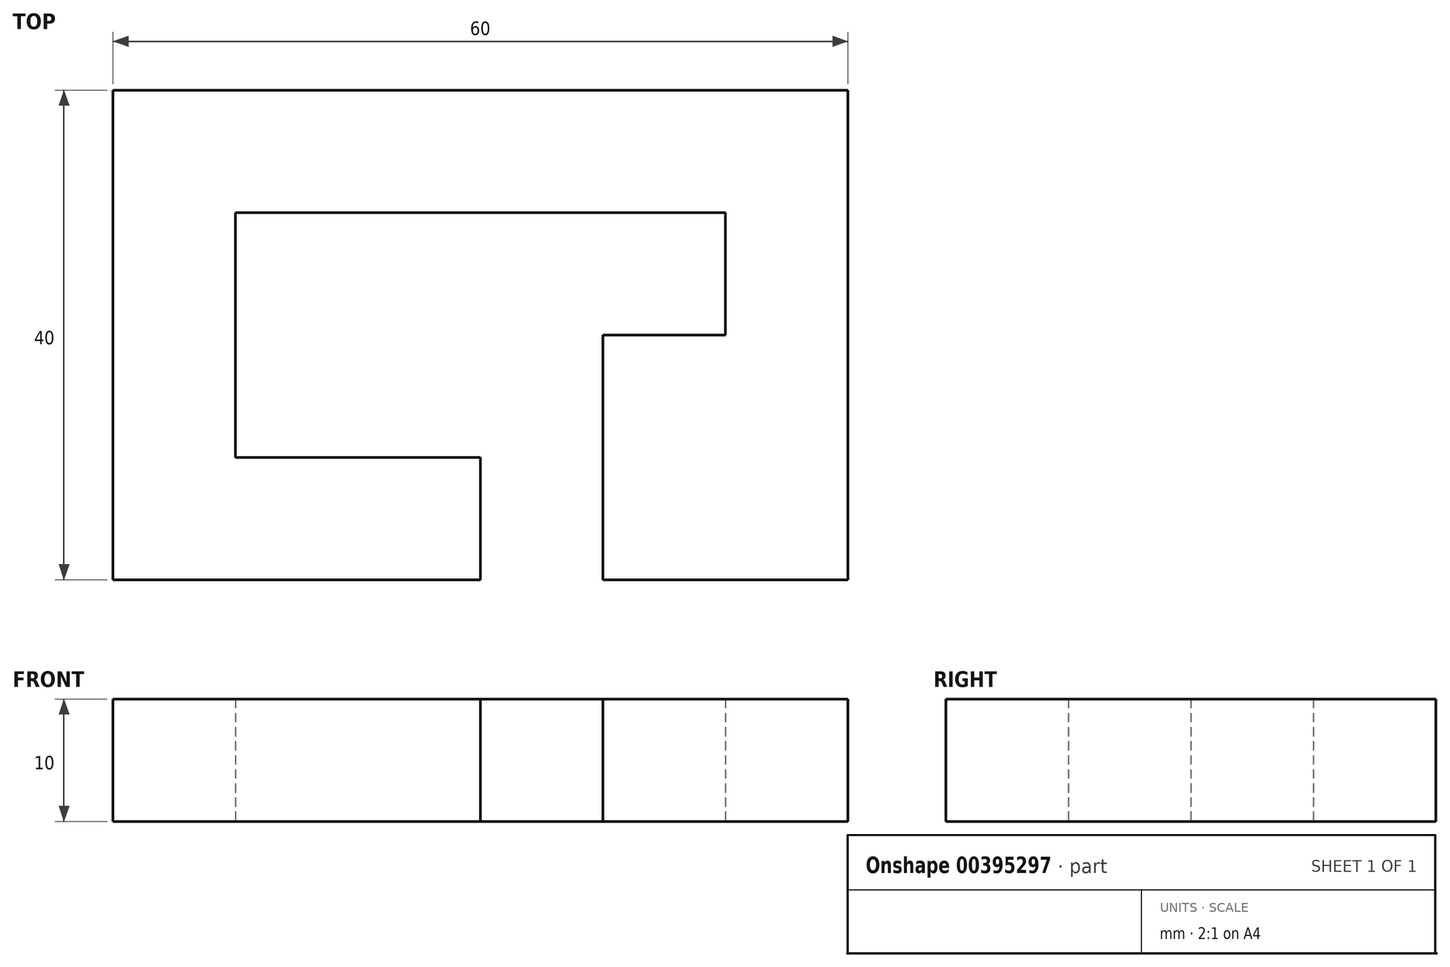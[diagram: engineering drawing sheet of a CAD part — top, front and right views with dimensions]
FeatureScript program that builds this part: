
annotation { "Feature Type Name" : "Feature", "Feature Type Description" : "" }
export const myFeature = defineFeature(function(context is Context, id is Id, definition is map)
    precondition{}
    {
        {
            var Q0;
            Q0=qCreatedBy(makeId("Top.planeOp"),FACE);
            var sketch = newSketch(context, id + "F0", { "sketchPlane" : qUnion([Q0])});
            skLineSegment(sketch, "E0.bottom", {"start": v(-30, 20) * mm, "end": v(30, 20) * mm});
            skLineSegment(sketch, "E0.top", {"start": v(-30, -20) * mm, "end": v(30, -20) * mm});
            skLineSegment(sketch, "E0.left", {"start": v(-30, 20) * mm, "end": v(-30, -20) * mm});
            skLineSegment(sketch, "E0.right", {"start": v(30, 20) * mm, "end": v(30, -20) * mm});
            skPoint(sketch, "E0.middle", {"position": v(0, 0) * mm});
            skLineSegment(sketch, "E1.bottom", {"start": v(-20, 10) * mm, "end": v(20, 10) * mm});
            skLineSegment(sketch, "E1.top", {"start": v(-20, -10) * mm, "end": v(20, -10) * mm});
            skLineSegment(sketch, "E1.left", {"start": v(-20, 10) * mm, "end": v(-20, -10) * mm});
            skLineSegment(sketch, "E1.right", {"start": v(20, 10) * mm, "end": v(20, -10) * mm});
            skLineSegment(sketch, "E2", {"start": v(20, -10) * mm, "end": v(10, -10) * mm, "construction": true});
            skLineSegment(sketch, "E3", {"start": v(20, 0) * mm, "end": v(10, 0) * mm});
            skLineSegment(sketch, "E4", {"start": v(10, 0) * mm, "end": v(10, -10) * mm});
            skLineSegment(sketch, "E5", {"start": v(10, -10) * mm, "end": v(10, -20) * mm});
            skLineSegment(sketch, "E6", {"start": v(10, -10) * mm, "end": v(0, -10) * mm, "construction": true});
            skLineSegment(sketch, "E7", {"start": v(0, -10) * mm, "end": v(0, -20) * mm});
            skSolve(sketch);
        }
        {
            var Q0;
            Q0=makeQuery(id+"F0.imprint","IMPRINT",FACE,{"disambiguationData":[TD([[makeQuery(id+"F0.imprint","IMPRINT",EDGE,{"derivedFrom":sQuery(id+"F0.wireOp",EDGE,"E0.bottom")}),-1.0]])]});
            var Q1;
            {var subQ4=sQuery(id+"F0.wireOp",EDGE,"E3");Q1=makeQuery(id+"F0.imprint","IMPRINT",FACE,{"disambiguationData":[TD([[makeQuery(id+"F0.imprint","IMPRINT",EDGE,{"derivedFrom":subQ4}),1.0]])]});}
            extrude(context, id + "F1", {"entities" : qUnion([Q0, Q1]), "depth" : 10 * mm});
        }
    });
